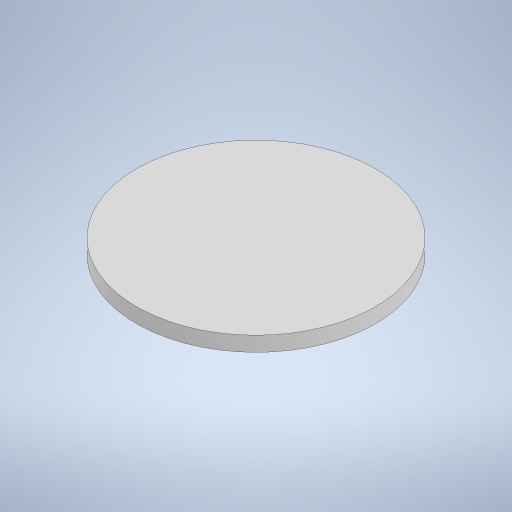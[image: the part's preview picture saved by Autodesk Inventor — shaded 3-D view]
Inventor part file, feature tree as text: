
AUTODESK INVENTOR PART (.ipt)
format: ipt  version: 2024.1 (Build 281209000, 209)  size: 334,848 bytes
history: native  units: in
note: dims shown in document units (in); Inventor stores cm internally (conversion verified against a paired STEP export)
features: extrude x2, sketch x2, mirror x1
ambient origin geometry x8: Origin, YZ Plane, XZ Plane, XY Plane, X Axis, Y Axis, Z Axis, Center Point
bodies: Solid1 (feature_tree)
feature tree (5):
  extrude  "Extrusion1"  Depth=0.062in TaperAngle=0.0deg
  extrude  "Extrusion2"  Depth=0.0709in
  mirror  "Mirror1"
  sketch  "Sketch1"  dims[d0=1.0in d1=0.062in d2=0.0in]
  sketch  "Sketch2"  dims[d3=0.73in d4=0.0787in d5=0.0394in d6=0.0197in d7=0.0394in d8=0.0197in d9=0.0394in d10=0.0197in d11=0.0394in d12=0.0197in d13=0.0394in d14=0.0197in d15=0.0394in d16=0.0197in d17=0.0787in d18=0.0787in d19=0.0787in d20=0.0709in d21=0.0in]
